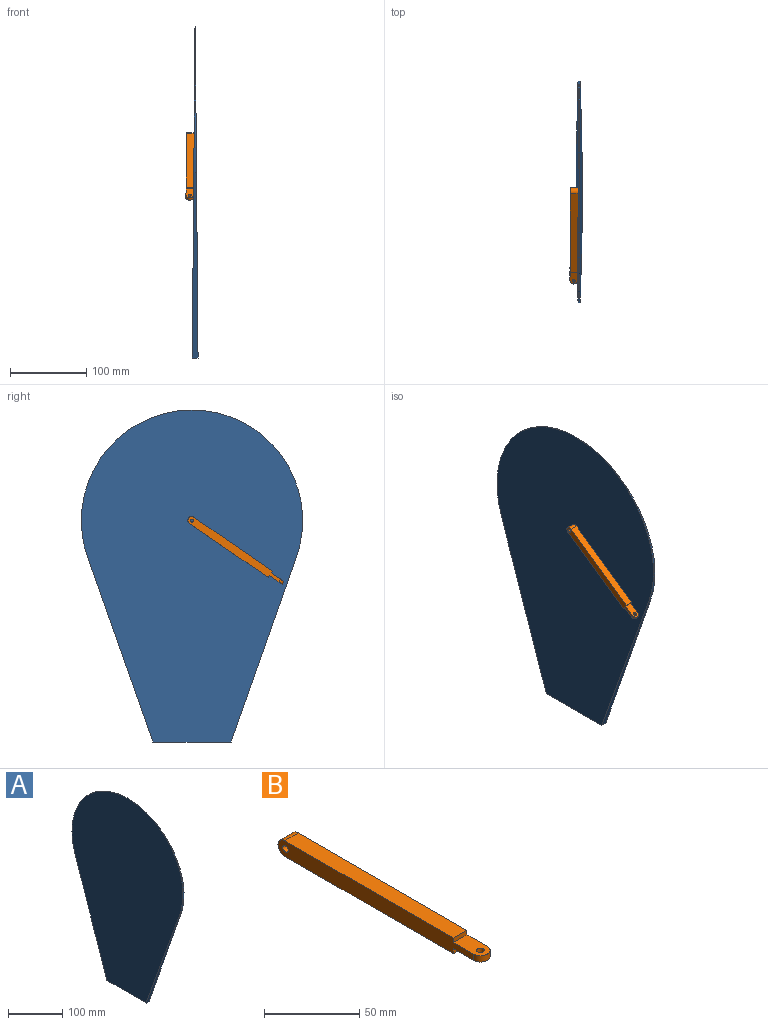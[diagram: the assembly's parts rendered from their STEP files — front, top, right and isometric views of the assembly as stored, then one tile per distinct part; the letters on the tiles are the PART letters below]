
ASSEMBLY  parts=2 mates=2
PART A: 8 faces, bbox 7.6x290x435 mm
  f0: plane 435x290mm, normal (-1,0,0.01), area 92208.5mm2, adj f1,f2,f3,f4,f5,f6
  f1: plane 242.7x85.81mm, normal (0,0.94,-0.33), area 1431.5mm2, adj f0,f2,f6,f7
  f2: plane 102.53x7.58mm, normal (0,0,-1), area 777.5mm2, adj f0,f1,f3,f7
  f3: plane 242.7x85.81mm, normal (0,-0.94,-0.33), area 1431.5mm2, adj f0,f2,f4,f7
  f4: plane 3.54x0mm, normal (0,0,1), area 0mm2, adj f0,f3,f5,f7
  f5: cylinder r=145mm len=290mm, axis (1,0,0), area 855.2mm2, adj f0,f4,f6,f7
  f6: plane 3.54x0mm, normal (0,0,1), area 0mm2, adj f0,f1,f5,f7
  f7: plane 435x290mm, normal (1,0,0.01), area 92208.5mm2, adj f1,f2,f3,f4,f5,f6
PART B: 12 faces, bbox 10x150x10 mm
  f0: plane 145x10mm, normal (-1,0,0), area 1336.7mm2, adj f2,f3,f4,f5,f6,f7,f8,f9
  f1: plane 145x10mm, normal (1,0,0), area 1336.7mm2, adj f2,f3,f4,f5,f6,f7,f8,f9
  f2: plane 125x10mm, normal (0,0,1), area 1250mm2, adj f0,f1,f4,f9
  f3: plane 125x10mm, normal (0,0,-1), area 1250mm2, adj f0,f1,f7,f9
  f4: plane 10x2.8mm, normal (0,-1,0), area 28mm2, adj f0,f1,f2,f5
  f5: plane 20x10mm, normal (0,0,1), area 176.7mm2, adj f0,f1,f4,f8,f10
  f6: plane 20x10mm, normal (0,0,-1), area 176.7mm2, adj f0,f1,f7,f8,f10
  f7: plane 10x3.2mm, normal (0,-1,0), area 32mm2, adj f0,f1,f3,f6
  f8: cylinder r=5mm len=10mm, axis (0,0,1), area 62.8mm2, adj f0,f1,f5,f6
  f9: cylinder r=5mm len=10mm, axis (-1,0,0), area 157.1mm2, adj f0,f1,f2,f3
  f10: cylinder r=2mm len=4mm, axis (0,0,1), area 50.2mm2, adj f5,f6
  f11: cylinder r=2mm len=10mm, axis (-1,0,0), area 125.7mm2, adj f0,f1
PLACE A t=(-27.09,280.05,-181.47)mm fixed
PLACE B rot(axis=(1,0.01,0),34.4deg) t=(-38.47,112.44,252.62)mm
MATE planar A.f0 <-> B.f1  axis (-1,0,0.01) through (-28.46,105.05,253.53)mm
MATE cylindrical A.f0 <-> B.f11  axis (-1,0,0.01) through (-28.46,105.05,253.53)mm
